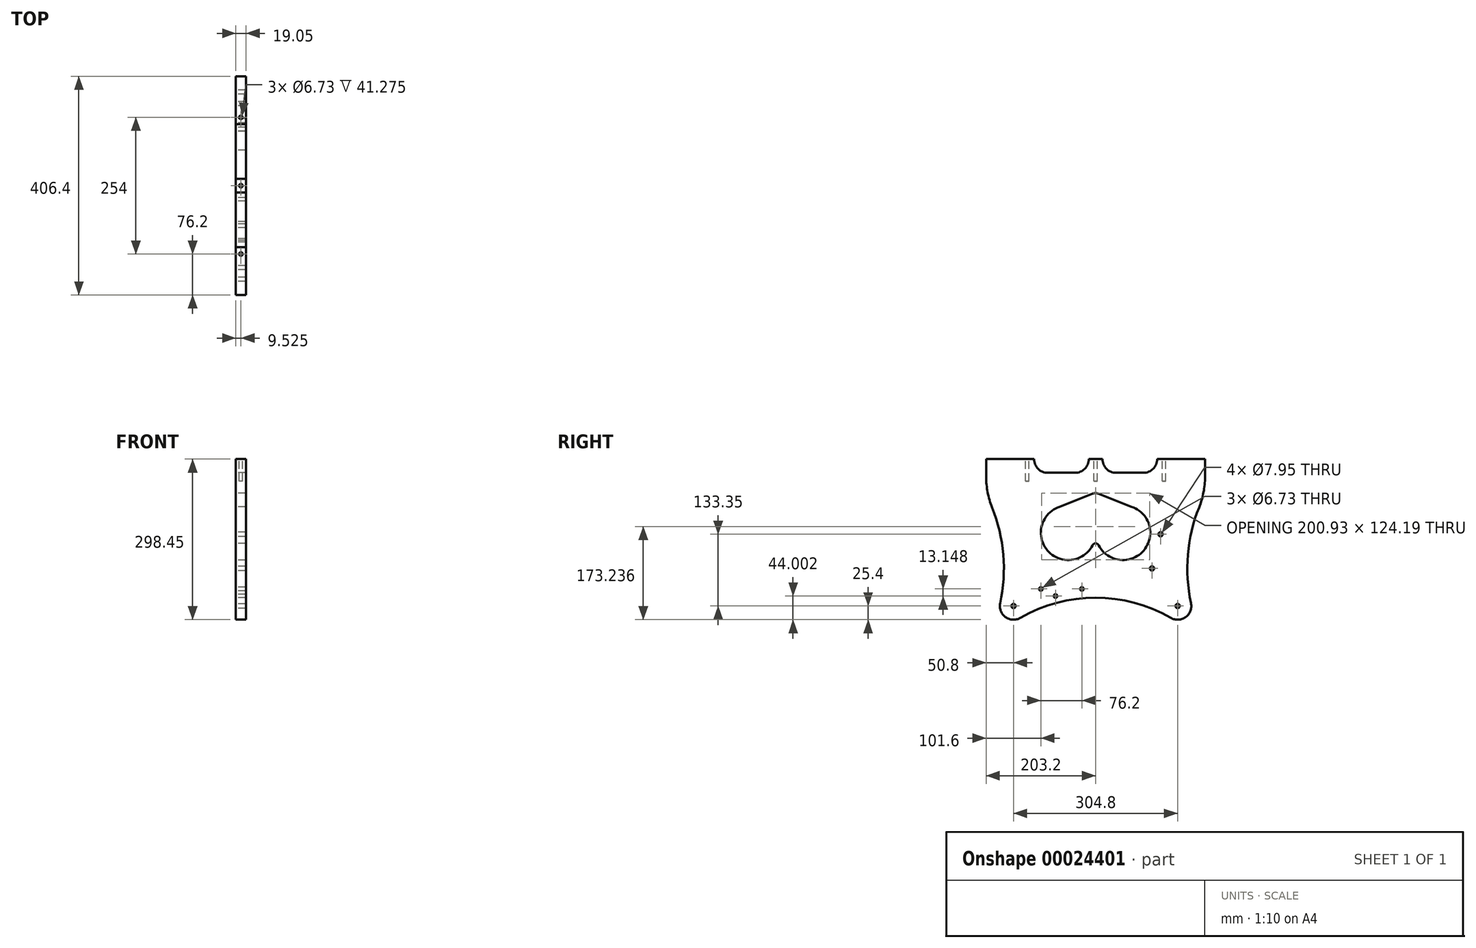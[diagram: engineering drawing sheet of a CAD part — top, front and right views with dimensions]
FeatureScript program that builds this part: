
annotation { "Feature Type Name" : "Feature", "Feature Type Description" : "" }
export const myFeature = defineFeature(function(context is Context, id is Id, definition is map)
    precondition{}
    {
        {
            var Q0;
            Q0=qCreatedBy(makeId("Right.planeOp"),FACE);
            var sketch = newSketch(context, id + "F0", { "sketchPlane" : qUnion([Q0])});
            skLineSegment(sketch, "E0.bottom", {"start": v(0, 0) * mm, "end": v(406.4, 0) * mm, "construction": true});
            skLineSegment(sketch, "E0.top", {"start": v(0, 298.45) * mm, "end": v(88.9, 298.45) * mm});
            skLineSegment(sketch, "E0.left", {"start": v(0, 0) * mm, "end": v(0, 265.48) * mm, "construction": true});
            skLineSegment(sketch, "E0.right", {"start": v(406.4, 0) * mm, "end": v(406.4, 265.48) * mm, "construction": true});
            skCircle(sketch, "E1", {"center": v(101.6, 57.15) * mm, "radius": 3.37 * mm});
            skCircle(sketch, "E2", {"center": v(177.8, 57.15) * mm, "radius": 3.37 * mm});
            skCircle(sketch, "E3", {"center": v(50.8, 25.4) * mm, "radius": 3.98 * mm});
            skCircle(sketch, "E4", {"center": v(355.6, 25.4) * mm, "radius": 3.98 * mm});
            skLineSegment(sketch, "E5", {"start": v(101.6, 57.15) * mm, "end": v(177.8, 57.15) * mm, "construction": true});
            skArc(sketch, "E6", {"start": v(342.88, 3.41) * mm, "mid": v(370.56, 4.87) * mm, "end": v(380.43, 30.77) * mm});
            skArc(sketch, "E7", {"start": v(25.97, 30.77) * mm, "mid": v(35.84, 4.87) * mm, "end": v(63.52, 3.41) * mm});
            skLineSegment(sketch, "E8", {"start": v(203.2, 0) * mm, "end": v(203.2, 40.9) * mm, "construction": true});
            skArc(sketch, "E9", {"start": v(348.62, 0) * mm, "mid": v(203.2, 40.9) * mm, "end": v(57.78, 0) * mm});
            skArc(sketch, "E10", {"start": v(395.44, 208.74) * mm, "mid": v(374.6, 120.88) * mm, "end": v(380.43, 30.77) * mm});
            skArc(sketch, "E11", {"start": v(25.97, 30.77) * mm, "mid": v(31.8, 120.88) * mm, "end": v(10.96, 208.74) * mm});
            skArc(sketch, "E12", {"start": v(395.44, 208.74) * mm, "mid": v(403.64, 236.58) * mm, "end": v(406.4, 265.48) * mm});
            skArc(sketch, "E13", {"start": v(0, 265.48) * mm, "mid": v(2.76, 236.58) * mm, "end": v(10.96, 208.74) * mm});
            skLineSegment(sketch, "E14", {"start": v(406.4, 265.48) * mm, "end": v(406.4, 298.45) * mm});
            skLineSegment(sketch, "E15", {"start": v(0, 265.48) * mm, "end": v(0, 298.45) * mm});
            skArc(sketch, "E16", {"start": v(208.84, 138.34) * mm, "mid": v(292.77, 128.8) * mm, "end": v(269.5, 210) * mm});
            skLineSegment(sketch, "E17", {"start": v(152.4, 161.62) * mm, "end": v(254, 161.62) * mm, "construction": true});
            skArc(sketch, "E18", {"start": v(208.84, 138.34) * mm, "mid": v(203.2, 141.79) * mm, "end": v(197.56, 138.34) * mm});
            skLineSegment(sketch, "E19", {"start": v(203.2, 161.62) * mm, "end": v(203.2, 135.44) * mm, "construction": true});
            skLineSegment(sketch, "E20", {"start": v(203.2, 161.62) * mm, "end": v(203.2, 222.63) * mm, "construction": true});
            skArc(sketch, "E21", {"start": v(207.88, 234.43) * mm, "mid": v(203.2, 235.33) * mm, "end": v(198.52, 234.43) * mm});
            skLineSegment(sketch, "E22", {"start": v(130.53, 207.47) * mm, "end": v(198.52, 234.43) * mm});
            skLineSegment(sketch, "E23", {"start": v(275.87, 207.47) * mm, "end": v(207.88, 234.43) * mm});
            skLineSegment(sketch, "E24", {"start": v(130.53, 207.47) * mm, "end": v(275.87, 207.47) * mm, "construction": true});
            skArc(sketch, "E25.trimOffspring", {"start": v(136.9, 210) * mm, "mid": v(113.63, 128.8) * mm, "end": v(197.56, 138.34) * mm});
            skLineSegment(sketch, "E26", {"start": v(203.2, 298.45) * mm, "end": v(215.9, 298.45) * mm});
            skLineSegment(sketch, "E27", {"start": v(190.5, 298.45) * mm, "end": v(190.5, 298.45) * mm});
            skLineSegment(sketch, "E28", {"start": v(165.1, 273.05) * mm, "end": v(114.3, 273.05) * mm});
            skLineSegment(sketch, "E29", {"start": v(88.9, 298.45) * mm, "end": v(88.9, 298.45) * mm});
            skLineSegment(sketch, "E30", {"start": v(215.9, 298.45) * mm, "end": v(215.9, 298.45) * mm});
            skLineSegment(sketch, "E31", {"start": v(241.3, 273.05) * mm, "end": v(292.1, 273.05) * mm});
            skLineSegment(sketch, "E32", {"start": v(317.5, 298.45) * mm, "end": v(317.5, 298.45) * mm});
            skPoint(sketch, "E33.visualSharp", {"position": v(88.9, 273.05) * mm});
            skArc(sketch, "E33.filletArc", {"start": v(88.9, 298.45) * mm, "mid": v(96.34, 280.49) * mm, "end": v(114.3, 273.05) * mm});
            skPoint(sketch, "E34.visualSharp", {"position": v(190.5, 273.05) * mm});
            skArc(sketch, "E34.filletArc", {"start": v(165.1, 273.05) * mm, "mid": v(183.06, 280.49) * mm, "end": v(190.5, 298.45) * mm});
            skPoint(sketch, "E35.visualSharp", {"position": v(215.9, 273.05) * mm});
            skArc(sketch, "E35.filletArc", {"start": v(215.9, 298.45) * mm, "mid": v(223.34, 280.49) * mm, "end": v(241.3, 273.05) * mm});
            skPoint(sketch, "E36.visualSharp", {"position": v(317.5, 273.05) * mm});
            skArc(sketch, "E36.filletArc", {"start": v(292.1, 273.05) * mm, "mid": v(310.06, 280.49) * mm, "end": v(317.5, 298.45) * mm});
            skLineSegment(sketch, "E37", {"start": v(88.9, 298.45) * mm, "end": v(190.5, 298.45) * mm, "construction": true});
            skLineSegment(sketch, "E38", {"start": v(190.5, 298.45) * mm, "end": v(203.2, 298.45) * mm});
            skLineSegment(sketch, "E39", {"start": v(215.9, 298.45) * mm, "end": v(317.5, 298.45) * mm, "construction": true});
            skLineSegment(sketch, "E40", {"start": v(317.5, 298.45) * mm, "end": v(406.4, 298.45) * mm});
            skCircle(sketch, "E41", {"center": v(128.73, 44) * mm, "radius": 3.37 * mm});
            skLineSegment(sketch, "E42", {"start": v(128.73, 44) * mm, "end": v(177.8, 57.15) * mm, "construction": true});
            skCircle(sketch, "E43", {"center": v(323.85, 158.75) * mm, "radius": 3.98 * mm});
            skCircle(sketch, "E44", {"center": v(307.98, 95.25) * mm, "radius": 3.98 * mm});
            skSolve(sketch);
        }
        {
            var Q0;
            Q0 = qSketchRegion(id + "F0", true);
            extrude(context, id + "F1", {"entities" : qUnion([Q0]), "depth" : 19.05 * mm});
        }
        {
            var Q0;
            Q0=makeQuery(id+"F1.opExtrude","SWEPT_FACE",FACE,{"disambiguationData":[OSD([sQuery(id+"F0.wireOp",EDGE,"E0.top")])]});
            var sketch = newSketch(context, id + "F2", { "sketchPlane" : qUnion([Q0])});
            skLineSegment(sketch, "E45", {"start": v(9.53, 0) * mm, "end": v(9.53, 203.2) * mm, "construction": true});
            skLineSegment(sketch, "E46", {"start": v(9.53, 203.2) * mm, "end": v(9.53, 406.4) * mm, "construction": true});
            skCircle(sketch, "E47", {"center": v(9.53, 203.2) * mm, "radius": 3.37 * mm});
            skCircle(sketch, "E48", {"center": v(9.52, 330.2) * mm, "radius": 3.37 * mm});
            skCircle(sketch, "E49", {"center": v(9.53, 76.2) * mm, "radius": 3.37 * mm});
            skSolve(sketch);
        }
        {
            var Q0;
            Q0 = qSketchRegion(id + "F2", true);
            extrude(context, id + "F3", {"entities" : qUnion([Q0]), "operationType" : NewBodyOperationType.REMOVE, "oppositeDirection" : true, "depth" : 41.27 * mm});
        }
    });
